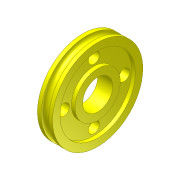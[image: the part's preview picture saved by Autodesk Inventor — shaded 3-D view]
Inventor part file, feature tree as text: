
AUTODESK INVENTOR PART (.ipt)
format: ipt  version: unknown  size: 237,568 bytes
history: native  units: in
note: dims shown in document units (in); Inventor stores cm internally (conversion verified against a paired STEP export)
features: sketch x3, revolve x1, extrude x1, pattern_circular x1
ambient origin geometry x8: Origin, YZ Plane, XZ Plane, XY Plane, X Axis, Y Axis, Z Axis, Center Point
feature tree (6):
  revolve  "Revolution1"  [1 undecoded]
  extrude  "Extrusion3"  Depth=0.0787in
  pattern_circular  "Circular Pattern3"  [2 undecoded]
  sketch  "Sketch5"  dims[d5=90.0deg d24=0.0394in d25=0.0394in d34=0.0197in d35=0.0394in d39=0.1575in d40=0.0591in d41=0.3937in d42=0.0in d43=1.5748in d44=360.0deg d46=0.0in d47=0.6299in]
  sketch  "Sketch1"  dims[d0=0.2362in d1=0.0394in]
  sketch  "Sketch4"  dims[d2=0.2756in d3=0.0394in d4=0.0787in]
note: 3 required parameter values undecoded (feature->parameter linkage not recoverable at this tier; creation-order binding heuristic only, values carry confidence <= 0.55)